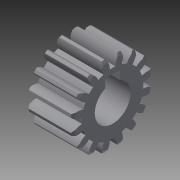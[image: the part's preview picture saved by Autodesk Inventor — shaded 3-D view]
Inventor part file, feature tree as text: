
AUTODESK INVENTOR PART (.ipt)
format: ipt  version: 2014 SP1 (Build 180222100, 222)  size: 287,744 bytes
history: native  units: in
note: dims shown in document units (in); Inventor stores cm internally (conversion verified against a paired STEP export)
features: chamfer x1, other x1, imported_body x1
ambient origin geometry x8: Origin, YZ Plane, XZ Plane, XY Plane, X Axis, Y Axis, Z Axis, Center Point
bodies: Body1 (feature_tree)
feature tree (3):
  chamfer  "Chamfer2"  [1 undecoded]
  other  "16T-10mmKeyBoreAM-20881"
  imported_body  "Base1"
note: 1 required parameter value undecoded (feature->parameter linkage not recoverable at this tier; creation-order binding heuristic only, values carry confidence <= 0.55)
